# Revit family: HOB_GEN_Cottesloe_Standard
name_source: partatom
category: Generic Models
units: mm (PartAtom-declared; Revit-internal decimal feet)

## family parameters
Always vertical = Yes
Can host rebar = No
Cut with Voids When Loaded = No
Maintain Annotation Orientation = No
Part Type = Normal
Room Calculation Point = No
Round Connector Dimension = Use Diameter
Shared = Yes
Work Plane-Based = No

## types (1)
- Cottesloe Standard 396x1830
    BattenDepth = 20 mm
    BattenSpacing = 56 mm
    BattenWidth = 20 mm
    Battens Material = Bamboo_horizontalGrain
    BattensBottomOffset = 0 mm  [stored 0 ft]
    BattensTopOffset = 0 mm  [stored 0 ft]
    Cost = 286 $
    Default Elevation = 0 mm  [stored 0 ft]
    Description = 28x40 mm slat / 396 mm standard width / 1830/2440 mm Standard height
    Manufacturer = HOB
    Model = Cottesloe Stanndard
    PanelCost = 300 $
    RailBottomOffset = 50 mm  [stored 0.164042 ft]
    RailTopOffset = 50 mm  [stored 0.164042 ft]
    SideOffset = 29 mm  [stored 0.0951444 ft]
    Support Rail Material = HOB_Black
    URL = https://houseofbamboo.com.au

note: [stored X ft] marks values corroborated as IEEE doubles in the binary element streams (Revit-internal decimal feet)

## geometry (parser evidence)
native form markers: Sweep x6
no freeform markers — native parametric forms only
